# Revit family: E SONNIGER - HEATER - MIX 1, MIX 2
name_source: partatom
category: Wyposażenie mechaniczne
revit_build: Autodesk Revit 2018 (Build: 20170927_1515(x64)
units: mm (PartAtom-declared; Revit-internal decimal feet)

## family parameters
Klasyfikacja = Brak
Obiekt nadrzędny = Powierzchnia
Punkt obliczania pomieszczeń = Nie
Tnij formami wycięć po wczytaniu = Nie
Typ części = Normalny
Współdzielony = Nie
Wymiar okrągłego złącza = Użyj średnicy

## types (2) — shared parameters
Domyślna rzędna = 1219.200 mm
IP class protection = IP54
O = 130.000 mm
Producent = SONNIGER Polska Sp. z o.o. Sp. k.
material = 230,230,230
max installation height = 15.000 mm
max working area = 380 m²
min installation height = 9.000 mm
min working area = 200 m²
power supply voltage = 230 V
zero-valued in all types: noise level

## per-type parameters (varying)
| type | H | Model | O1 | Opis | S g | W g | max air output | motor power | motor speed | operating noise level | weight with water | weight without water |
| MIX 1 - wall mounting | 13536.341 mm | Mix 1 | Tak | Nagrzewnica Heater MIX 1 | 19500.000 mm | 19500.000 mm | 4800.0 m³/h | 250 W | 1350 | speed I 36 dB(A) / speed II 44 dB(A) / speed III 54 dB (A) | 9.20 kg | 9.20 kg |
| MIX 2 - wall mounting | 16560.341 mm | Mix 2 | Nie | Nagrzewnica Heater MIX 2 | 21200.000 mm | 21200.000 mm | 7200.0 m³/h | 520 W | 1380 | speed I 31 dB(A) / speed II 42 dB(A) / speed III 49 dB (A) | 15.80 kg | 15.80 kg |
